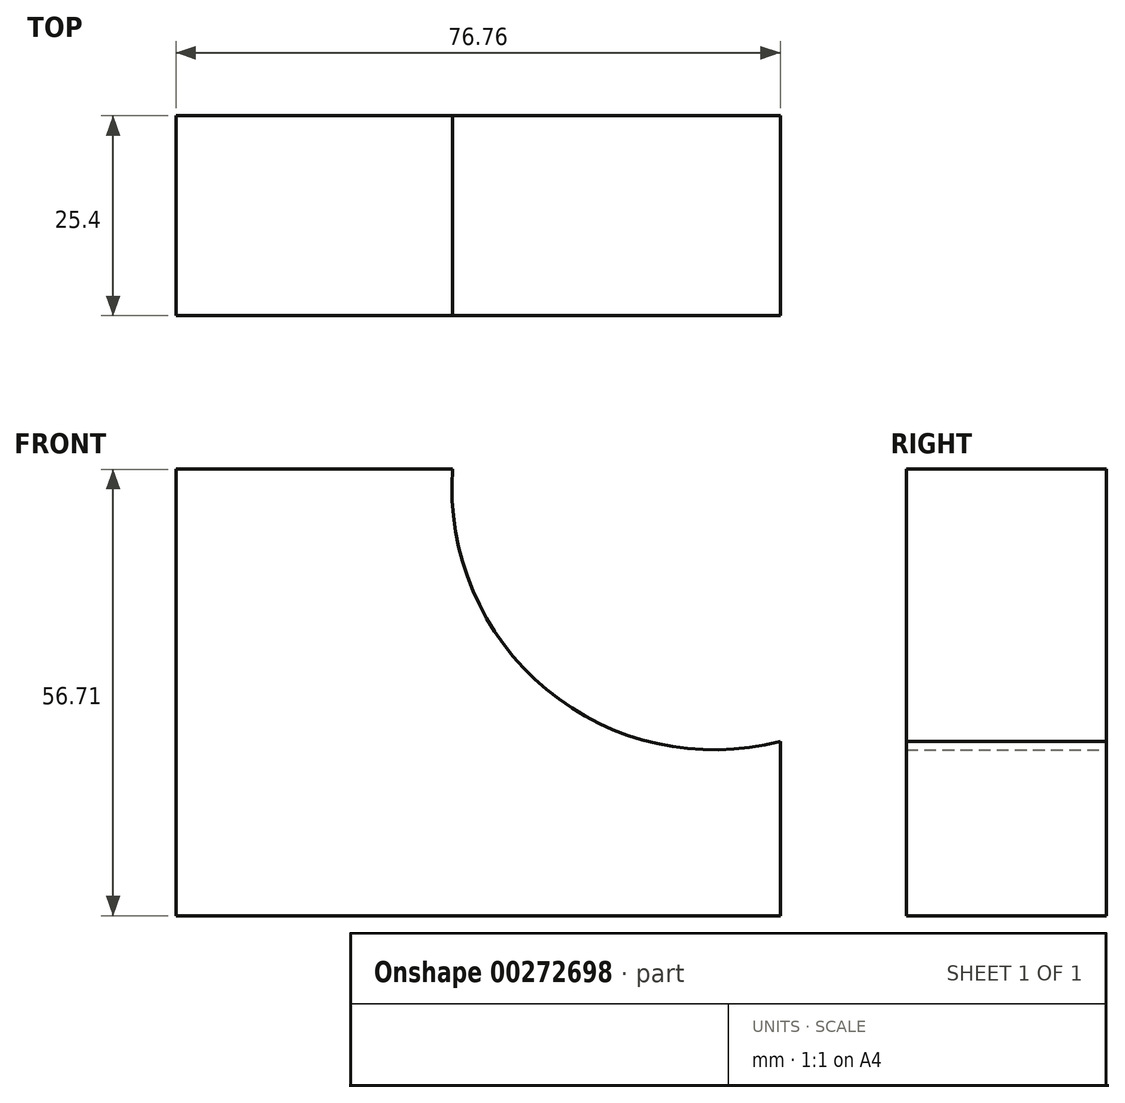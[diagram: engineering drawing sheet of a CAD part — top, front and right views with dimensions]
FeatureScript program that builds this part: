
annotation { "Feature Type Name" : "Feature", "Feature Type Description" : "" }
export const myFeature = defineFeature(function(context is Context, id is Id, definition is map)
    precondition{}
    {
        {
            var Q0;
            Q0=qCreatedBy(makeId("Front.planeOp"),FACE);
            var sketch = newSketch(context, id + "F0", { "sketchPlane" : qUnion([Q0])});
            skLineSegment(sketch, "E0", {"start": v(0, 0) * mm, "end": v(-76.76, 0) * mm});
            skLineSegment(sketch, "E1", {"start": v(-76.76, 0) * mm, "end": v(-76.76, 56.71) * mm});
            skLineSegment(sketch, "E2", {"start": v(-76.76, 56.71) * mm, "end": v(-41.63, 56.71) * mm});
            skLineSegment(sketch, "E3", {"start": v(0, 0) * mm, "end": v(0, 22.15) * mm});
            skArc(sketch, "E4", {"start": v(-41.63, 56.71) * mm, "mid": v(-29.7, 28.74) * mm, "end": v(0, 22.15) * mm});
            skSolve(sketch);
        }
        {
            var Q0;
            Q0=makeQuery(id+"F0.imprint","IMPRINT",FACE,{"disambiguationData":[TD([[makeQuery(id+"F0.imprint","IMPRINT",EDGE,{"derivedFrom":sQuery(id+"F0.wireOp",EDGE,"E0")}),-1.0]])]});
            extrude(context, id + "F1", {"entities" : qUnion([Q0]), "depth" : 25.4 * mm});
        }
    });
